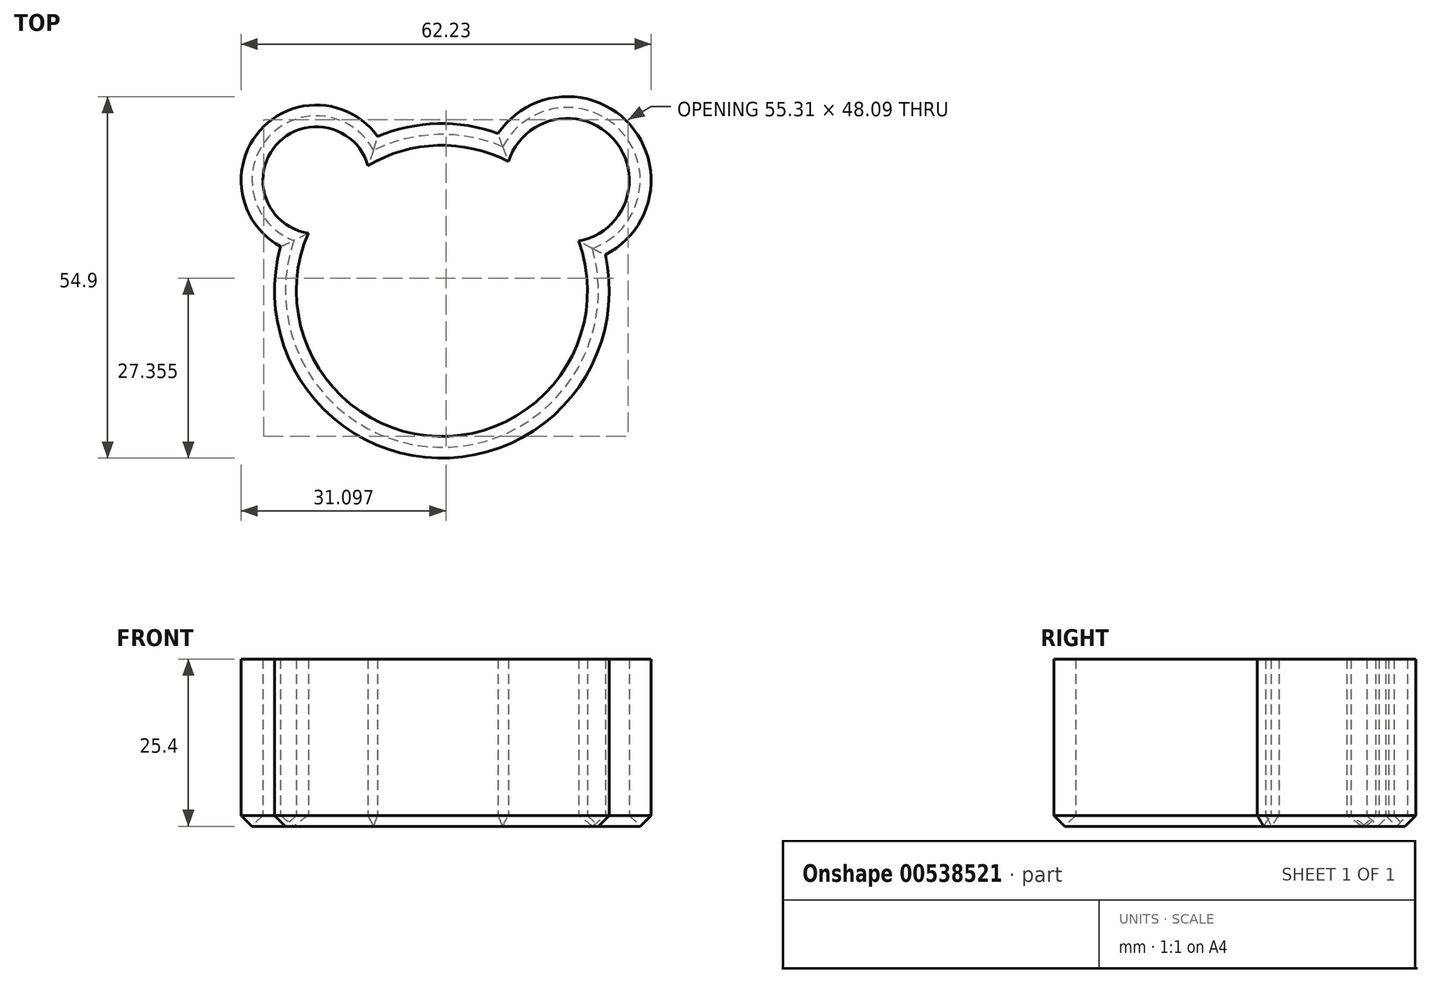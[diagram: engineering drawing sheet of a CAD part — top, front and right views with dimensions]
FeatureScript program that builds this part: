
annotation { "Feature Type Name" : "Feature", "Feature Type Description" : "" }
export const myFeature = defineFeature(function(context is Context, id is Id, definition is map)
    precondition{}
    {
        {
            var Q0;
            Q0=qCreatedBy(makeId("Top.planeOp"),FACE);
            var sketch = newSketch(context, id + "F0", { "sketchPlane" : qUnion([Q0])});
            skArc(sketch, "E0", {"start": v(8.54, 23.92) * mm, "mid": v(-0.65, 25.4) * mm, "end": v(-9.75, 23.45) * mm});
            skArc(sketch, "E1", {"start": v(24.8, 5.48) * mm, "mid": v(28.58, 25.2) * mm, "end": v(8.54, 23.92) * mm});
            skLineSegment(sketch, "E2", {"start": v(-19.05, 16.8) * mm, "end": v(19.05, 16.8) * mm, "construction": true});
            skLineSegment(sketch, "E3", {"start": v(0, 0) * mm, "end": v(19.05, 16.8) * mm, "construction": true});
            skLineSegment(sketch, "E4", {"start": v(-19.05, 16.8) * mm, "end": v(0, 0) * mm, "construction": true});
            skArc(sketch, "E5.trimOffspring", {"start": v(-9.75, 23.45) * mm, "mid": v(-27.62, 24.36) * mm, "end": v(-24.49, 6.75) * mm});
            skArc(sketch, "E6.trimOffspring", {"start": v(-24.49, 6.75) * mm, "mid": v(-0.65, -25.4) * mm, "end": v(24.8, 5.48) * mm});
            skArc(sketch, "E7.0", {"start": v(-11.23, 19.03) * mm, "mid": v(-25.15, 22.18) * mm, "end": v(-20.28, 8.77) * mm});
            skArc(sketch, "E7.1", {"start": v(10.1, 19.66) * mm, "mid": v(-0.65, 22.09) * mm, "end": v(-11.23, 19.03) * mm});
            skArc(sketch, "E7.2", {"start": v(20.76, 7.56) * mm, "mid": v(26.1, 23.02) * mm, "end": v(10.1, 19.66) * mm});
            skArc(sketch, "E7.3", {"start": v(-20.28, 8.77) * mm, "mid": v(-0.65, -22.09) * mm, "end": v(20.76, 7.56) * mm});
            skSolve(sketch);
        }
        {
            var Q0;
            Q0=makeQuery(id+"F0.imprint","IMPRINT",FACE,{"disambiguationData":[TD([[makeQuery(id+"F0.imprint","IMPRINT",EDGE,{"derivedFrom":sQuery(id+"F0.wireOp",EDGE,"E0")}),1.0]])]});
            extrude(context, id + "F1", {"entities" : qUnion([Q0]), "depth" : 25.4 * mm, "offsetDistance" : 25.4 * mm});
        }
        {
            var Q0;
            Q0=makeQuery(id+"F1.opExtrude","CAP_EDGE",EDGE,{"disambiguationData":[OSD([sQuery(id+"F0.wireOp",EDGE,"E6.trimOffspring")])],"isStart":true});
            var Q1;
            Q1=makeQuery(id+"F1.opExtrude","CAP_EDGE",EDGE,{"disambiguationData":[OSD([sQuery(id+"F0.wireOp",EDGE,"E7.3")])],"isStart":true});
            var Q2;
            Q2=makeQuery(id+"F1.opExtrude","CAP_EDGE",EDGE,{"disambiguationData":[OSD([sQuery(id+"F0.wireOp",EDGE,"E7.0")])],"isStart":true});
            var Q3;
            Q3=makeQuery(id+"F1.opExtrude","CAP_EDGE",EDGE,{"disambiguationData":[OSD([sQuery(id+"F0.wireOp",EDGE,"E5.trimOffspring")])],"isStart":true});
            var Q4;
            Q4=makeQuery(id+"F1.opExtrude","CAP_EDGE",EDGE,{"disambiguationData":[OSD([sQuery(id+"F0.wireOp",EDGE,"E7.1")])],"isStart":true});
            var Q5;
            Q5=makeQuery(id+"F1.opExtrude","CAP_EDGE",EDGE,{"disambiguationData":[OSD([sQuery(id+"F0.wireOp",EDGE,"E0")])],"isStart":true});
            var Q6;
            Q6=makeQuery(id+"F1.opExtrude","CAP_FACE",FACE,{"disambiguationData":[OSD([sQuery(id+"F0.wireOp",EDGE,"E0"),sQuery(id+"F0.wireOp",EDGE,"E1"),sQuery(id+"F0.wireOp",EDGE,"E5.trimOffspring"),sQuery(id+"F0.wireOp",EDGE,"E6.trimOffspring"),sQuery(id+"F0.wireOp",EDGE,"E7.0"),sQuery(id+"F0.wireOp",EDGE,"E7.1"),sQuery(id+"F0.wireOp",EDGE,"E7.2"),sQuery(id+"F0.wireOp",EDGE,"E7.3")])],"isStart":true});
            chamfer(context, id + "F2", {"entities" : qUnion([Q0, Q1, Q2, Q3, Q4, Q5, Q6]), "width" : 1.65 * mm, "tangentPropagation" : true});
        }
    });
